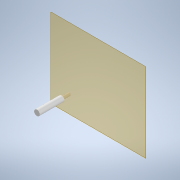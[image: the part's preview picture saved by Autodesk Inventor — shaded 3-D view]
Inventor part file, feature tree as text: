
AUTODESK INVENTOR PART (.ipt)
format: ipt  version: 2020 (Build 240168000, 168)  size: 103,424 bytes
history: native  units: in
note: dims shown in document units (in); Inventor stores cm internally (conversion verified against a paired STEP export)
features: other x6, plane x2, extrude x2, sketch x2, reference x1
ambient origin geometry x8: Origin, YZ Plane, XZ Plane, XY Plane, X Axis, Y Axis, Z Axis, Center Point
bodies: Solid1 (feature_tree)
feature tree (13):
  plane  "Work Plane1"
  extrude  "Extrusion1"  Depth=0.25in
  plane  "Work Plane2"
  extrude  "Extrusion3"  [1 undecoded]
  sketch  "Sketch1"  dims[d0=0.25in d1=0.0in d5=0.1772in]
  reference  "Reference1"
  sketch  "Sketch2"  dims[d6=0.7874in d7=0.0in]
  other  "<userpath>\Documents\Inventor\Drone\Assembly.iam"
  other  "Assembly.iam"
  other  "Frame:1"
  other  "DJI F330 qoadrotor arm:1"
  other  "DJI F330 qoadrotor arm v2"
  other  "holder:1"
note: 1 required parameter value undecoded (feature->parameter linkage not recoverable at this tier; creation-order binding heuristic only, values carry confidence <= 0.55)
